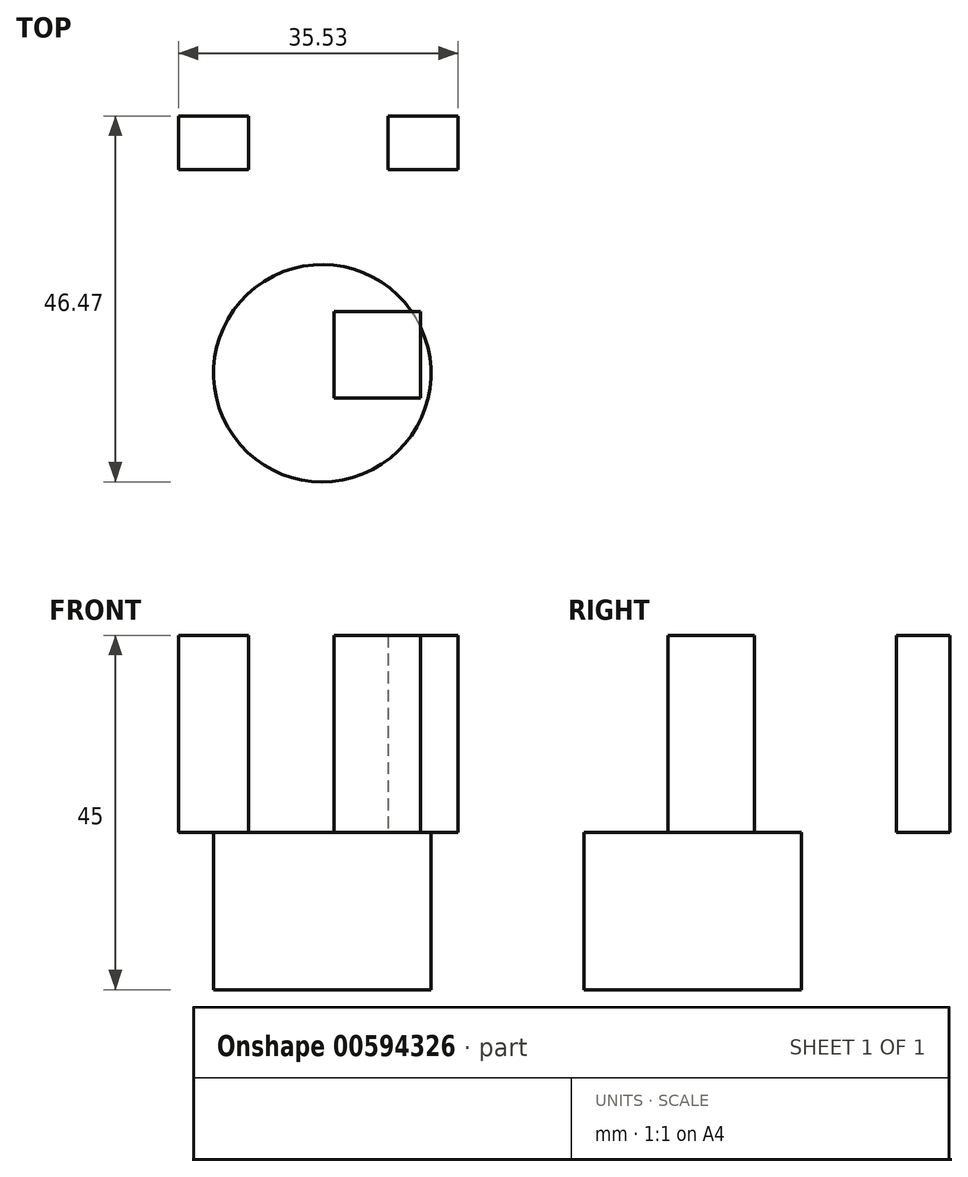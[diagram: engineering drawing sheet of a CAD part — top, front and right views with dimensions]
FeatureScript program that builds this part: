
annotation { "Feature Type Name" : "Feature", "Feature Type Description" : "" }
export const myFeature = defineFeature(function(context is Context, id is Id, definition is map)
    precondition{}
    {
        {
            var Q0;
            Q0=qCreatedBy(makeId("Top.planeOp"),FACE);
            var sketch = newSketch(context, id + "F0", { "sketchPlane" : qUnion([Q0])});
            skCircle(sketch, "E0", {"center": v(-11.93, 5.96) * mm, "radius": 13.8 * mm});
            skSolve(sketch);
        }
        {
            var Q0;
            Q0=makeQuery(id+"F0.imprint","IMPRINT",FACE,{"disambiguationData":[TD([[makeQuery(id+"F0.imprint","IMPRINT",EDGE,{"derivedFrom":sQuery(id+"F0.wireOp",EDGE,"E0")}),1.0]])]});
            extrude(context, id + "F1", {"entities" : qUnion([Q0]), "depth" : 20 * mm, "offsetDistance" : 25.4 * mm});
        }
        {
            var Q0;
            Q0=makeQuery(id+"F1.opExtrude","CAP_FACE",FACE,{"disambiguationData":[OSD([sQuery(id+"F0.wireOp",EDGE,"E0")])],"isStart":false});
            var sketch = newSketch(context, id + "F2", { "sketchPlane" : qUnion([Q0])});
            skLineSegment(sketch, "E1.bottom", {"start": v(-30.2, 38.63) * mm, "end": v(-21.32, 38.63) * mm});
            skLineSegment(sketch, "E1.top", {"start": v(-30.2, 31.83) * mm, "end": v(-21.32, 31.83) * mm});
            skLineSegment(sketch, "E1.left", {"start": v(-30.2, 38.63) * mm, "end": v(-30.2, 31.83) * mm});
            skLineSegment(sketch, "E1.right", {"start": v(-21.32, 38.63) * mm, "end": v(-21.32, 31.83) * mm});
            skPoint(sketch, "E2.firstSnap0", {"position": v(-25.76, 38.63) * mm});
            skLineSegment(sketch, "E2.bottom", {"start": v(-3.55, 38.63) * mm, "end": v(5.33, 38.63) * mm});
            skLineSegment(sketch, "E2.top", {"start": v(-3.55, 31.83) * mm, "end": v(5.33, 31.83) * mm});
            skLineSegment(sketch, "E2.left", {"start": v(-3.55, 38.63) * mm, "end": v(-3.55, 31.83) * mm});
            skLineSegment(sketch, "E2.right", {"start": v(5.33, 38.63) * mm, "end": v(5.33, 31.83) * mm});
            skSolve(sketch);
        }
        {
            var Q0;
            Q0 = qSketchRegion(id + "F2", true);
            extrude(context, id + "F3", {"entities" : qUnion([Q0]), "depth" : 25 * mm, "offsetDistance" : 25 * mm});
        }
        {
            var Q0;
            Q0=makeQuery(id+"F1.opExtrude","CAP_FACE",FACE,{"disambiguationData":[OSD([sQuery(id+"F0.wireOp",EDGE,"E0")])],"isStart":false});
            var sketch = newSketch(context, id + "F4", { "sketchPlane" : qUnion([Q0])});
            skLineSegment(sketch, "E3", {"start": v(-11.93, 5.96) * mm, "end": v(1.88, 5.96) * mm, "construction": true});
            skLineSegment(sketch, "E4.right", {"start": v(-13.88, -3.55) * mm, "end": v(-4.92, 2.84) * mm});
            skLineSegment(sketch, "E5.bottom", {"start": v(-10.42, 13.84) * mm, "end": v(0.58, 13.84) * mm});
            skLineSegment(sketch, "E5.top", {"start": v(-10.42, 2.84) * mm, "end": v(0.58, 2.84) * mm});
            skLineSegment(sketch, "E5.left", {"start": v(-10.42, 13.84) * mm, "end": v(-10.42, 2.84) * mm});
            skLineSegment(sketch, "E5.right", {"start": v(0.58, 13.84) * mm, "end": v(0.58, 2.84) * mm});
            skPoint(sketch, "E6", {"position": v(-4.92, 2.84) * mm});
            skSolve(sketch);
        }
        {
            var Q0;
            Q0 = qSketchRegion(id + "F4", true);
            extrude(context, id + "F5", {"entities" : qUnion([Q0]), "operationType" : NewBodyOperationType.ADD, "depth" : 25 * mm, "offsetDistance" : 25 * mm});
        }
    });
